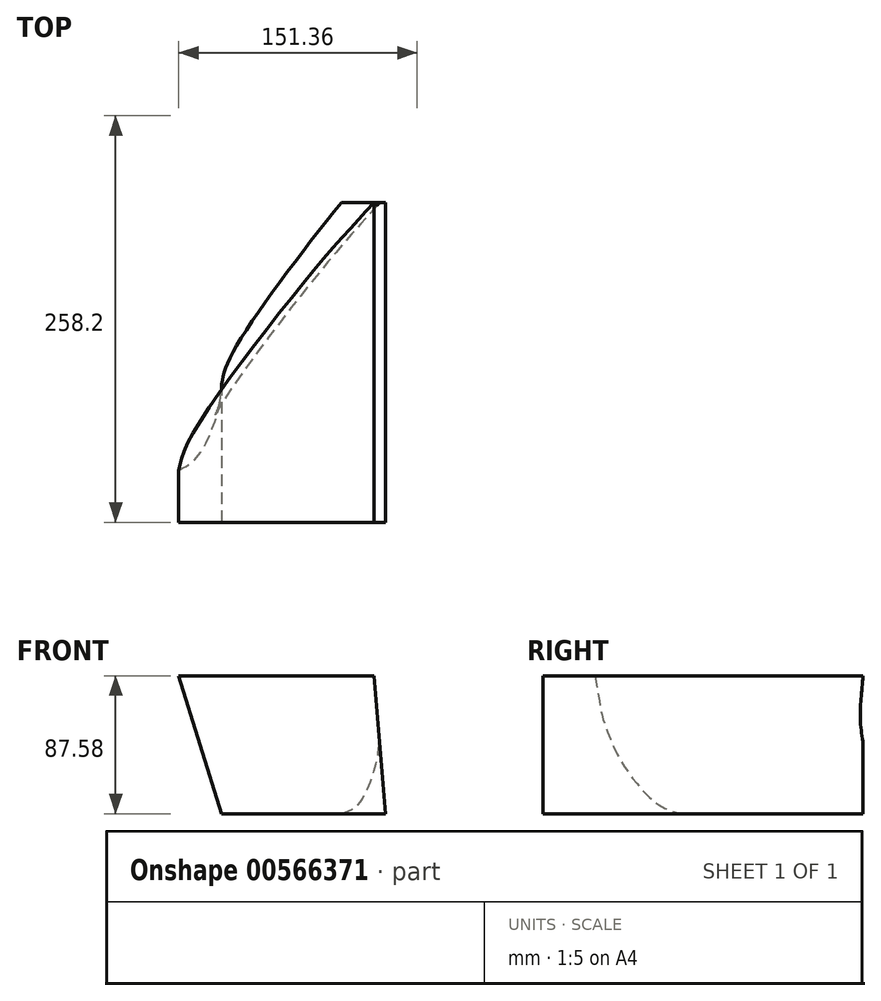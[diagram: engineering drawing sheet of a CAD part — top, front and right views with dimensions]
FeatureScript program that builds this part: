
annotation { "Feature Type Name" : "Feature", "Feature Type Description" : "" }
export const myFeature = defineFeature(function(context is Context, id is Id, definition is map)
    precondition{}
    {
        {
            var Q0;
            Q0=qCreatedBy(makeId("Front.planeOp"),FACE);
            cPlane(context, id + "F0", {"entities" : qUnion([Q0]), "cplaneType" : CPlaneType.OFFSET, "offset" : 33 * mm, "oppositeDirection" : true, "width" : 152.4 * mm, "height" : 152.4 * mm});
        }
        {
            var Q0;
            Q0=qCreatedBy(makeId("Front.planeOp"),FACE);
            var sketch = newSketch(context, id + "F1", { "sketchPlane" : qUnion([Q0])});
            skPoint(sketch, "E0", {"position": v(0, 0) * mm});
            skSolve(sketch);
        }
        {
            var Q0;
            Q0=qCreatedBy(id+"F0.planeOp",FACE);
            var sketch = newSketch(context, id + "F2", { "sketchPlane" : qUnion([Q0])});
            skPoint(sketch, "E1", {"position": v(-97.65, 85.15) * mm});
            skSolve(sketch);
        }
        {
            var Q0;
            Q0=qCreatedBy(makeId("Front.planeOp"),FACE);
            cPlane(context, id + "F3", {"entities" : qUnion([Q0]), "cplaneType" : CPlaneType.OFFSET, "offset" : (155 - 4.85 / 2) * mm, "oppositeDirection" : true, "width" : 152.4 * mm, "height" : 152.4 * mm});
        }
        {
            var Q0;
            Q0=qCreatedBy(id+"F3.planeOp",FACE);
            var sketch = newSketch(context, id + "F4", { "sketchPlane" : qUnion([Q0])});
            skPoint(sketch, "E2", {"position": v(-3, 87.58) * mm});
            skSolve(sketch);
        }
        {
            var Q0;
            Q0=qCreatedBy(makeId("Front.planeOp"),FACE);
            var sketch = newSketch(context, id + "F5", { "sketchPlane" : qUnion([Q0])});
            skPoint(sketch, "E3", {"position": v(14.68, 0) * mm});
            skLineSegment(sketch, "E4", {"start": v(-3, 87.58) * mm, "end": v(7.32, 87.58) * mm, "construction": true});
            skLineSegment(sketch, "E5", {"start": v(7.32, 87.58) * mm, "end": v(14.68, 0) * mm});
            skLineSegment(sketch, "E6", {"start": v(7.32, 87.58) * mm, "end": v(-113.08, 87.58) * mm});
            skLineSegment(sketch, "E7", {"start": v(14.68, 0) * mm, "end": v(-89.33, 0) * mm});
            skLineSegment(sketch, "E8", {"start": v(-89.33, 0) * mm, "end": v(-116.67, 87.57) * mm});
            skLineSegment(sketch, "E9", {"start": v(-116.67, 87.58) * mm, "end": v(-113.08, 87.58) * mm});
            skSolve(sketch);
        }
        {
            var Q0;
            Q0 = qSketchRegion(id + "F5", true);
            var Q1;
            Q1=qCreatedBy(id+"F3.planeOp",FACE);
            extrude(context, id + "F6", {"entities" : qUnion([Q0]), "oppositeDirection" : true, "depth" : 203.2 * mm, "endBoundEntityFace" : qUnion([Q1]), "offsetDistance" : 25.4 * mm});
        }
        {
            var Q0;
            Q0=makeQuery(id+"F6.opExtrude","SWEPT_FACE",FACE,{"disambiguationData":[OSD([sQuery(id+"F5.wireOp",EDGE,"E6"),sQuery(id+"F5.wireOp",EDGE,"E9")])]});
            var sketch = newSketch(context, id + "F7", { "sketchPlane" : qUnion([Q0])});
            skLineSegment(sketch, "E10", {"start": v(-3, 152.57) * mm, "end": v(-37, 152.57) * mm, "construction": true});
            skLineSegment(sketch, "E11", {"start": v(-97.65, 33) * mm, "end": v(-109.65, 53) * mm, "construction": true});
            skPoint(sketch, "E12", {"position": v(7.32, 203.2) * mm});
            skFitSpline(sketch, "E13", {"points": [v(7.32, 203.2) * mm, v(-37, 152.57) * mm, v(-109.65, 53) * mm, v(-116.67, 33) * mm], "startDerivative": vector(-112.8, -122.65) * mm, "endDerivative": vector(-15.42, -83.27) * mm});
            skLineSegment(sketch, "E14", {"start": v(-116.67, 33) * mm, "end": v(-97.26, 33) * mm, "construction": true});
            skLineSegment(sketch, "E15", {"start": v(-116.67, 33) * mm, "end": v(-116.67, 203.2) * mm});
            skLineSegment(sketch, "E16", {"start": v(-116.67, 203.2) * mm, "end": v(7.32, 203.2) * mm});
            skSolve(sketch);
        }
        {
            var Q0;
            Q0=makeQuery(id+"F6.opExtrude","SWEPT_FACE",FACE,{"disambiguationData":[OSD([sQuery(id+"F5.wireOp",EDGE,"E8")])]});
            var sketch = newSketch(context, id + "F8", { "sketchPlane" : qUnion([Q0])});
            skFitSpline(sketch, "E17", {"points": [v(-33, 118.37) * mm, v(-38.75, 87.59) * mm, v(-47.46, 65.6) * mm, v(-58.66, 47.91) * mm, v(-69.15, 35.99) * mm, v(-88, 26.63) * mm], "startDerivative": vector(-43.48, -262.3) * mm, "endDerivative": vector(-152.38, -35.58) * mm});
            skLineSegment(sketch, "E18", {"start": v(-33, 110.39) * mm, "end": v(-33, 118.37) * mm, "construction": true});
            skSolve(sketch);
        }
        {
            var Q0;
            Q0 = qSketchRegion(id + "F7", true);
            var Q1;
            Q1 = qConstructionFilter(qBodyType(qCreatedBy(id + "F8" ,EDGE), BodyType.WIRE), ConstructionObject.NO);
            sweep(context, id + "F9", {"operationType" : NewBodyOperationType.REMOVE, "profiles" : qUnion([Q0]), "path" : qUnion([Q1]), "keepProfileOrientation" : true});
        }
    });
